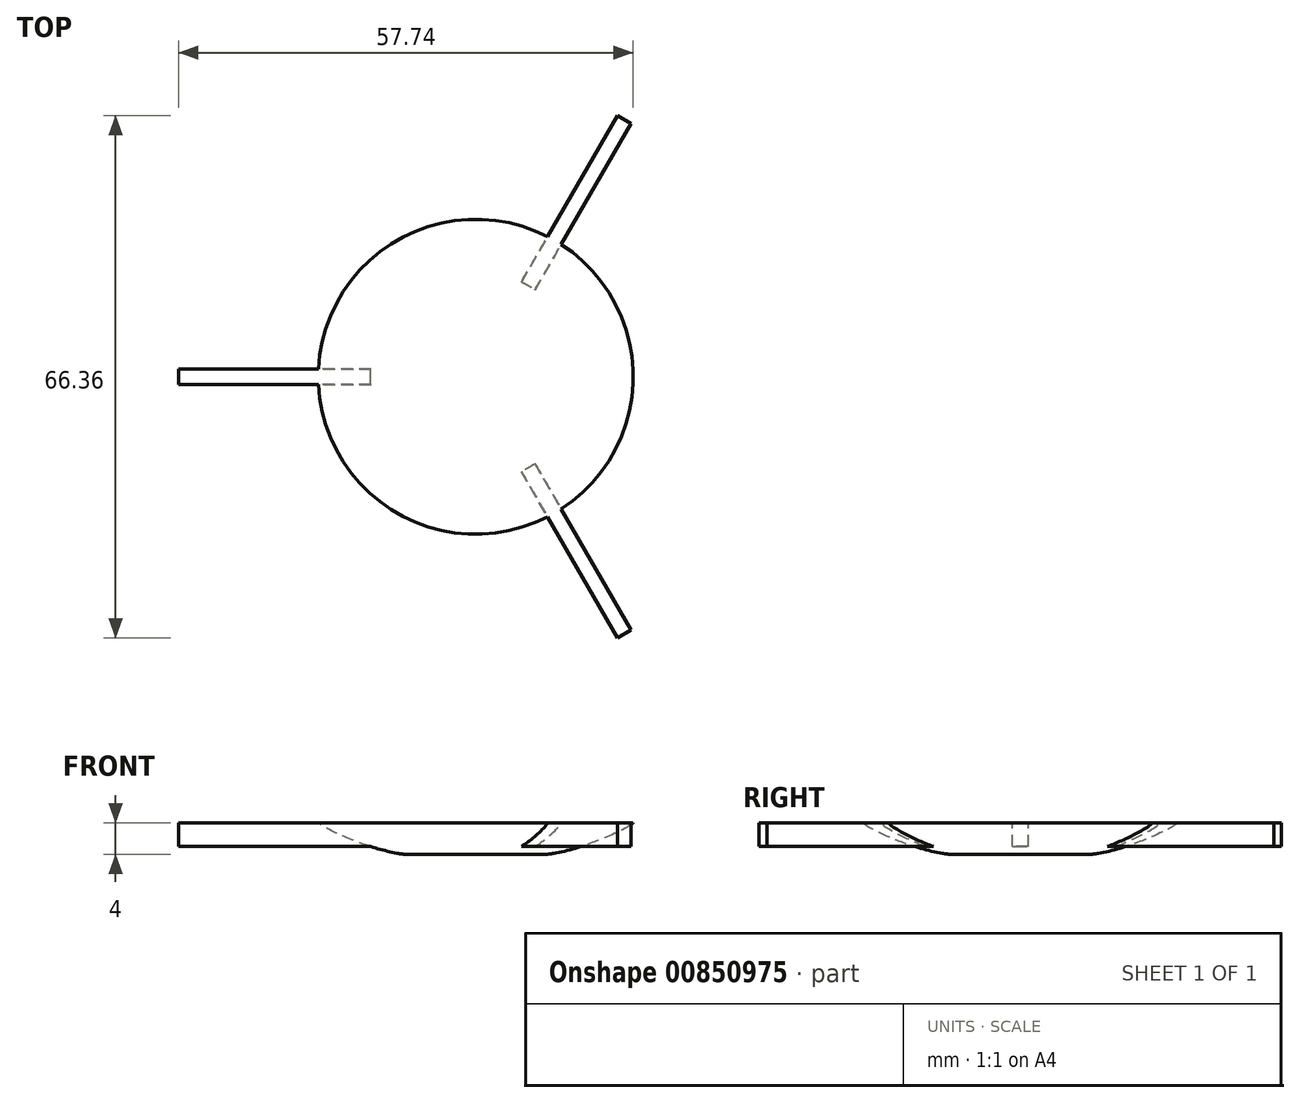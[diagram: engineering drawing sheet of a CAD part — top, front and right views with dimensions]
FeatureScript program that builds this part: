
annotation { "Feature Type Name" : "Feature", "Feature Type Description" : "" }
export const myFeature = defineFeature(function(context is Context, id is Id, definition is map)
    precondition{}
    {
        {
            var Q0;
            Q0=qCreatedBy(makeId("Top.planeOp"),FACE);
            var sketch = newSketch(context, id + "F0", { "sketchPlane" : qUnion([Q0])});
            skCircle(sketch, "E0", {"center": v(0, 0) * mm, "radius": 20 * mm});
            skSolve(sketch);
        }
        {
            var Q0;
            Q0=makeQuery(id+"F0.imprint","IMPRINT",FACE,{"disambiguationData":[TD([[makeQuery(id+"F0.imprint","IMPRINT",EDGE,{"derivedFrom":sQuery(id+"F0.wireOp",EDGE,"E0")}),1.0]])]});
            extrude(context, id + "F1", {"entities" : qUnion([Q0]), "depth" : 4 * mm, "offsetDistance" : 25 * mm});
        }
        {
            var Q0;
            Q0=makeQuery(id+"F1.opExtrude","CAP_FACE",FACE,{"disambiguationData":[OSD([sQuery(id+"F0.wireOp",EDGE,"E0")])],"isStart":true});
            fillet(context, id + "F2", {"entities" : qUnion([Q0]), "radius" : 18 * mm, "tangentPropagation" : true, "rho" : 0.3, "crossSection" : FilletCrossSection.CONIC, "allowEdgeOverflow" : false});
        }
        {
            var Q0;
            Q0=makeQuery(id+"F1.opExtrude","CAP_FACE",FACE,{"disambiguationData":[OSD([sQuery(id+"F0.wireOp",EDGE,"E0")])],"isStart":false});
            var sketch = newSketch(context, id + "F3", { "sketchPlane" : qUnion([Q0])});
            skLineSegment(sketch, "E1.bottom", {"start": v(-37.74, 1) * mm, "end": v(-12.74, 1) * mm});
            skLineSegment(sketch, "E1.top", {"start": v(-37.74, -1) * mm, "end": v(-12.74, -1) * mm});
            skLineSegment(sketch, "E1.left", {"start": v(-37.74, 1) * mm, "end": v(-37.74, -1) * mm});
            skLineSegment(sketch, "E1.right", {"start": v(-12.74, 1) * mm, "end": v(-12.74, -1) * mm});
            skPoint(sketch, "E1.middle", {"position": v(-25.24, 0) * mm});
            skLineSegment(sketch, "E2.1.0", {"start": v(18, -33.18) * mm, "end": v(5.5, -11.53) * mm});
            skPoint(sketch, "E2.1.1", {"position": v(12.62, -21.86) * mm});
            skLineSegment(sketch, "E2.1.2", {"start": v(19.74, -32.18) * mm, "end": v(7.24, -10.53) * mm});
            skLineSegment(sketch, "E2.1.3", {"start": v(5.5, -11.53) * mm, "end": v(7.24, -10.53) * mm});
            skLineSegment(sketch, "E2.1.4", {"start": v(18, -33.18) * mm, "end": v(19.74, -32.18) * mm});
            skLineSegment(sketch, "E2.2.0", {"start": v(19.74, 32.18) * mm, "end": v(7.24, 10.53) * mm});
            skPoint(sketch, "E2.2.1", {"position": v(12.62, 21.86) * mm});
            skLineSegment(sketch, "E2.2.2", {"start": v(18, 33.18) * mm, "end": v(5.5, 11.53) * mm});
            skLineSegment(sketch, "E2.2.3", {"start": v(7.24, 10.53) * mm, "end": v(5.5, 11.53) * mm});
            skLineSegment(sketch, "E2.2.4", {"start": v(19.74, 32.18) * mm, "end": v(18, 33.18) * mm});
            skPoint(sketch, "E2.center", {"position": v(0, 0) * mm});
            skSolve(sketch);
        }
        {
            var Q0;
            Q0=makeQuery(id+"F3.imprint","IMPRINT",FACE,{"disambiguationData":[TD([[makeQuery(id+"F3.imprint","IMPRINT",EDGE,{"derivedFrom":sQuery(id+"F3.wireOp",EDGE,"E1.bottom")}),-1.0]])]});
            var Q1;
            Q1=makeQuery(id+"F3.imprint","IMPRINT",FACE,{"disambiguationData":[TD([[makeQuery(id+"F3.imprint","IMPRINT",EDGE,{"derivedFrom":sQuery(id+"F3.wireOp",EDGE,"E2.1.0")}),-1.0]])]});
            var Q2;
            Q2=makeQuery(id+"F3.imprint","IMPRINT",FACE,{"disambiguationData":[TD([[makeQuery(id+"F3.imprint","IMPRINT",EDGE,{"derivedFrom":sQuery(id+"F3.wireOp",EDGE,"E2.2.0")}),-1.0]])]});
            extrude(context, id + "F4", {"entities" : qUnion([Q0, Q1, Q2]), "operationType" : NewBodyOperationType.ADD, "oppositeDirection" : true, "depth" : 3 * mm, "offsetDistance" : 25 * mm});
        }
    });
